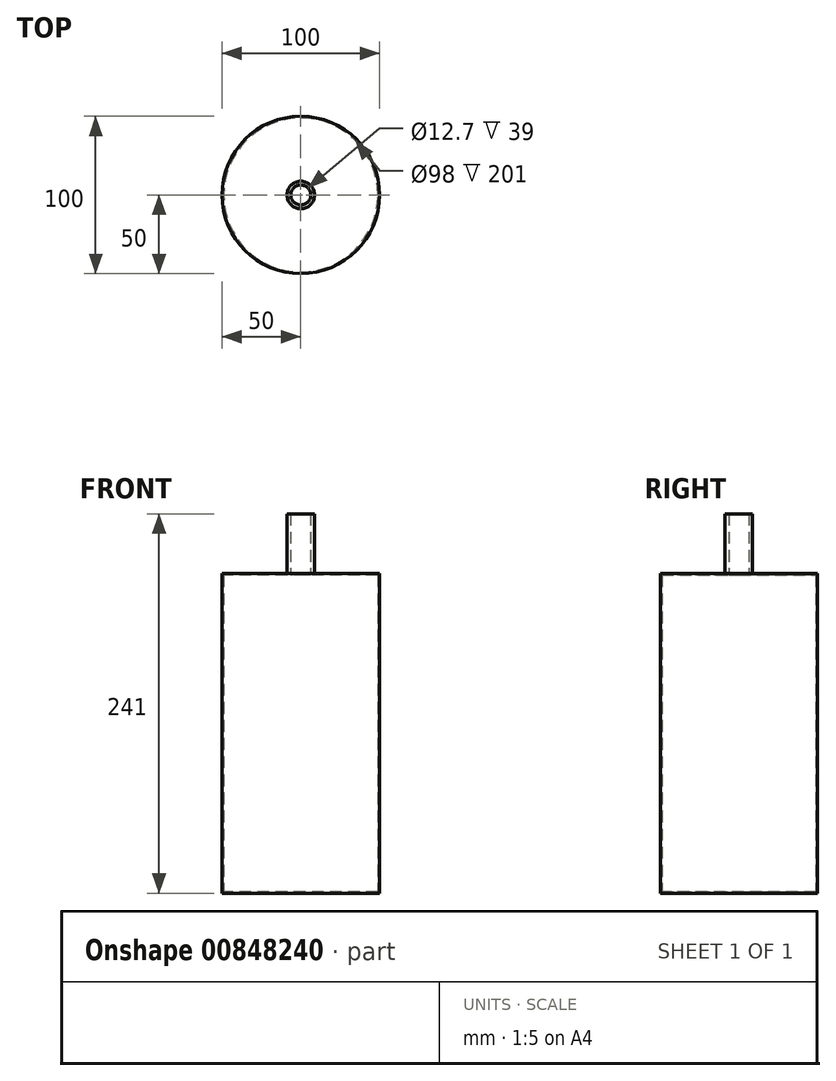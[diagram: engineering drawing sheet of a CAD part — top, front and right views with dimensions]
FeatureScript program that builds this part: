
annotation { "Feature Type Name" : "Feature", "Feature Type Description" : "" }
export const myFeature = defineFeature(function(context is Context, id is Id, definition is map)
    precondition{}
    {
        {
            var Q0;
            Q0=qCreatedBy(makeId("Top.planeOp"),FACE);
            var sketch = newSketch(context, id + "F0", { "sketchPlane" : qUnion([Q0])});
            skCircle(sketch, "E0", {"center": v(0, 0) * mm, "radius": 50 * mm});
            skCircle(sketch, "E1", {"center": v(0, 0) * mm, "radius": 49 * mm});
            skSolve(sketch);
        }
        {
            var Q0;
            Q0 = qSketchRegion(id + "F0", true);
            extrude(context, id + "F1", {"entities" : qUnion([Q0]), "depth" : 201 * mm, "offsetDistance" : 25 * mm});
        }
        {
            var Q0;
            Q0=makeQuery(id+"F1.opExtrude","CAP_FACE",FACE,{"disambiguationData":[OSD([sQuery(id+"F0.wireOp",EDGE,"E0"),sQuery(id+"F0.wireOp",EDGE,"E1")])],"isStart":true});
            var sketch = newSketch(context, id + "F2", { "sketchPlane" : qUnion([Q0])});
            skCircle(sketch, "E2", {"center": v(0, 0) * mm, "radius": 50 * mm});
            skPoint(sketch, "E2.first.point", {"position": v(-47.18, 16.57) * mm});
            skPoint(sketch, "E2.second.point", {"position": v(33.02, 37.54) * mm});
            skPoint(sketch, "E2.third.point", {"position": v(-18.77, -46.34) * mm});
            skSolve(sketch);
        }
        {
            var Q0;
            Q0 = qSketchRegion(id + "F2", true);
            extrude(context, id + "F3", {"entities" : qUnion([Q0]), "operationType" : NewBodyOperationType.ADD, "depth" : 1 * mm, "offsetDistance" : 25 * mm});
        }
        {
            var Q0;
            Q0=qCreatedBy(makeId("Top.planeOp"),FACE);
            cPlane(context, id + "F4", {"entities" : qUnion([Q0]), "cplaneType" : CPlaneType.OFFSET, "offset" : 201 * mm, "width" : 150 * mm, "height" : 150 * mm});
        }
        {
            var Q0;
            Q0=qCreatedBy(id+"F4.planeOp",FACE);
            var sketch = newSketch(context, id + "F5", { "sketchPlane" : qUnion([Q0])});
            skCircle(sketch, "E3", {"center": v(0, 0) * mm, "radius": 50 * mm});
            skCircle(sketch, "E4", {"center": v(0, 0) * mm, "radius": 6.35 * mm});
            skSolve(sketch);
        }
        {
            var Q0;
            Q0 = qSketchRegion(id + "F5", true);
            extrude(context, id + "F6", {"entities" : qUnion([Q0]), "operationType" : NewBodyOperationType.ADD, "depth" : 1 * mm, "offsetDistance" : 25 * mm});
        }
        {
            var Q0;
            Q0=qCreatedBy(id+"F4.planeOp",FACE);
            cPlane(context, id + "F7", {"entities" : qUnion([Q0]), "cplaneType" : CPlaneType.OFFSET, "offset" : 1 * mm, "width" : 150 * mm, "height" : 150 * mm});
        }
        {
            var Q0;
            Q0=qCreatedBy(id+"F7.planeOp",FACE);
            var sketch = newSketch(context, id + "F8", { "sketchPlane" : qUnion([Q0])});
            skCircle(sketch, "E5", {"center": v(0, 0) * mm, "radius": 6.35 * mm});
            skCircle(sketch, "E6", {"center": v(0, 0) * mm, "radius": 8.73 * mm});
            skSolve(sketch);
        }
        {
            var Q0;
            Q0 = qSketchRegion(id + "F8", true);
            extrude(context, id + "F9", {"entities" : qUnion([Q0]), "operationType" : NewBodyOperationType.ADD, "depth" : 38 * mm, "offsetDistance" : 25 * mm});
        }
    });
